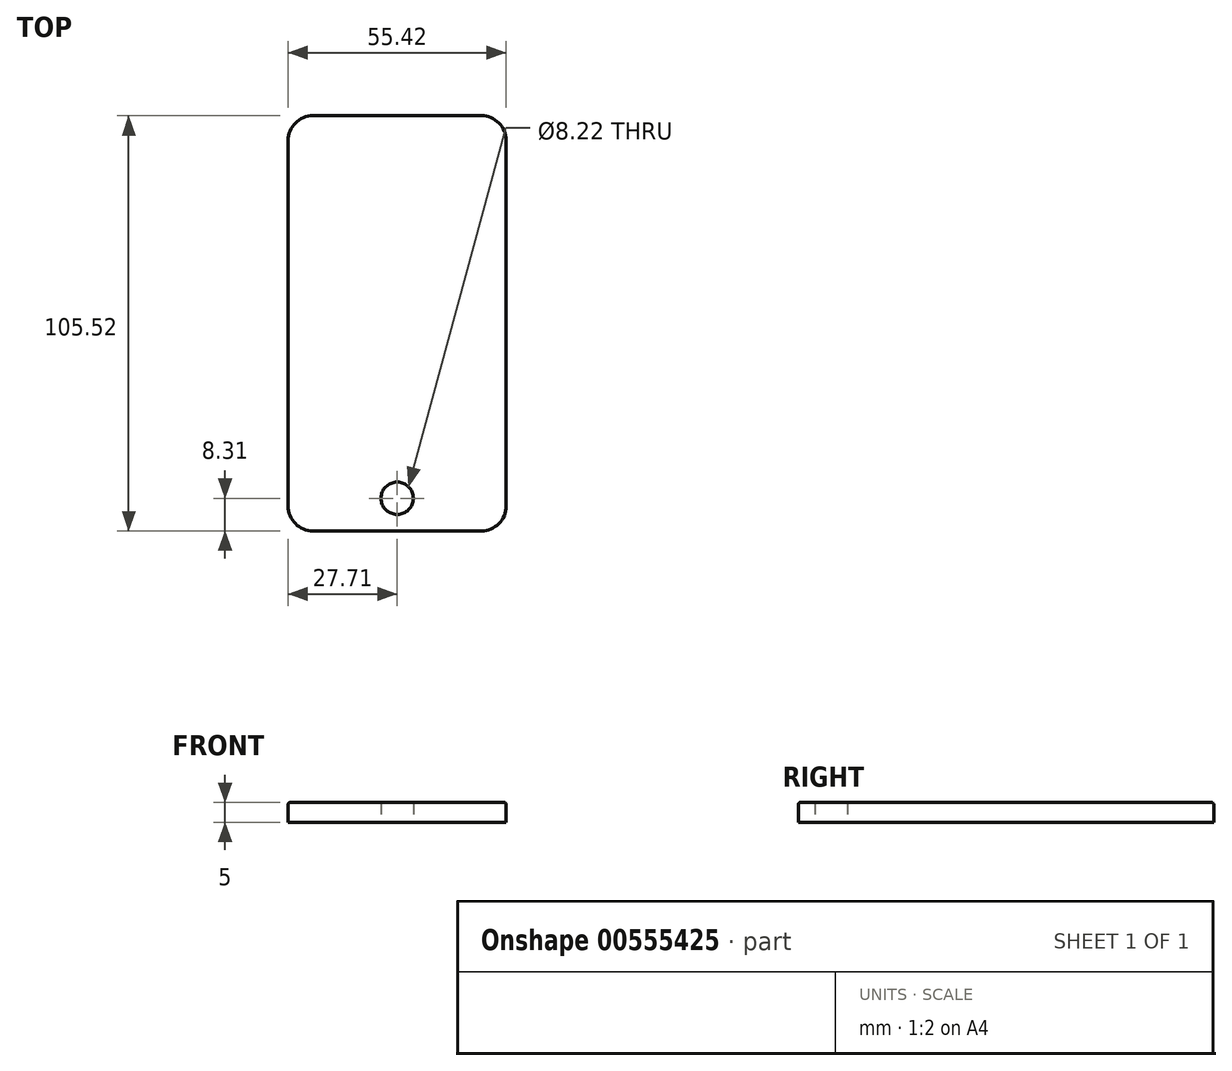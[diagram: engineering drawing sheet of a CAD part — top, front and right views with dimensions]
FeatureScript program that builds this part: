
annotation { "Feature Type Name" : "Feature", "Feature Type Description" : "" }
export const myFeature = defineFeature(function(context is Context, id is Id, definition is map)
    precondition{}
    {
        {
            var Q0;
            Q0=qCreatedBy(makeId("Top.planeOp"),FACE);
            var sketch = newSketch(context, id + "F0", { "sketchPlane" : qUnion([Q0])});
            skLineSegment(sketch, "E0.bottom", {"start": v(21.36, 52.76) * mm, "end": v(-21.36, 52.76) * mm});
            skLineSegment(sketch, "E0.top", {"start": v(21.36, -52.76) * mm, "end": v(-21.36, -52.76) * mm});
            skLineSegment(sketch, "E0.left", {"start": v(27.7, 46.41) * mm, "end": v(27.7, -46.41) * mm});
            skLineSegment(sketch, "E0.right", {"start": v(-27.7, 46.41) * mm, "end": v(-27.7, -46.41) * mm});
            skPoint(sketch, "E0.middle", {"position": v(0, 0) * mm});
            skPoint(sketch, "E1.visualSharp", {"position": v(-27.7, 52.76) * mm});
            skArc(sketch, "E1.filletArc", {"start": v(-21.36, 52.76) * mm, "mid": v(-25.85, 50.9) * mm, "end": v(-27.7, 46.41) * mm});
            skPoint(sketch, "E2.visualSharp", {"position": v(27.7, 52.76) * mm});
            skArc(sketch, "E2.filletArc", {"start": v(27.7, 46.41) * mm, "mid": v(25.85, 50.9) * mm, "end": v(21.36, 52.76) * mm});
            skPoint(sketch, "E3.visualSharp", {"position": v(27.7, -52.76) * mm});
            skArc(sketch, "E3.filletArc", {"start": v(21.36, -52.76) * mm, "mid": v(25.85, -50.9) * mm, "end": v(27.7, -46.41) * mm});
            skPoint(sketch, "E4.visualSharp", {"position": v(-27.7, -52.76) * mm});
            skArc(sketch, "E4.filletArc", {"start": v(-27.7, -46.41) * mm, "mid": v(-25.85, -50.9) * mm, "end": v(-21.36, -52.76) * mm});
            skCircle(sketch, "E5", {"center": v(0, -44.45) * mm, "radius": 4.11 * mm});
            skSolve(sketch);
        }
        {
            var Q0;
            Q0=makeQuery(id+"F0.imprint","IMPRINT",FACE,{"disambiguationData":[TD([[makeQuery(id+"F0.imprint","IMPRINT",EDGE,{"derivedFrom":sQuery(id+"F0.wireOp",EDGE,"E0.bottom")}),1.0]])]});
            extrude(context, id + "F1", {"entities" : qUnion([Q0]), "depth" : 5 * mm, "offsetDistance" : 25.4 * mm});
        }
        {
            var Q0;
            Q0=makeQuery(id+"F1.opExtrude","CAP_EDGE",EDGE,{"disambiguationData":[OSD([sQuery(id+"F0.wireOp",EDGE,"E4.filletArc")])],"isStart":false});
            fillet(context, id + "F2", {"entities" : qUnion([Q0]), "radius" : 0.5 * mm, "tangentPropagation" : true, "allowEdgeOverflow" : false});
        }
    });
